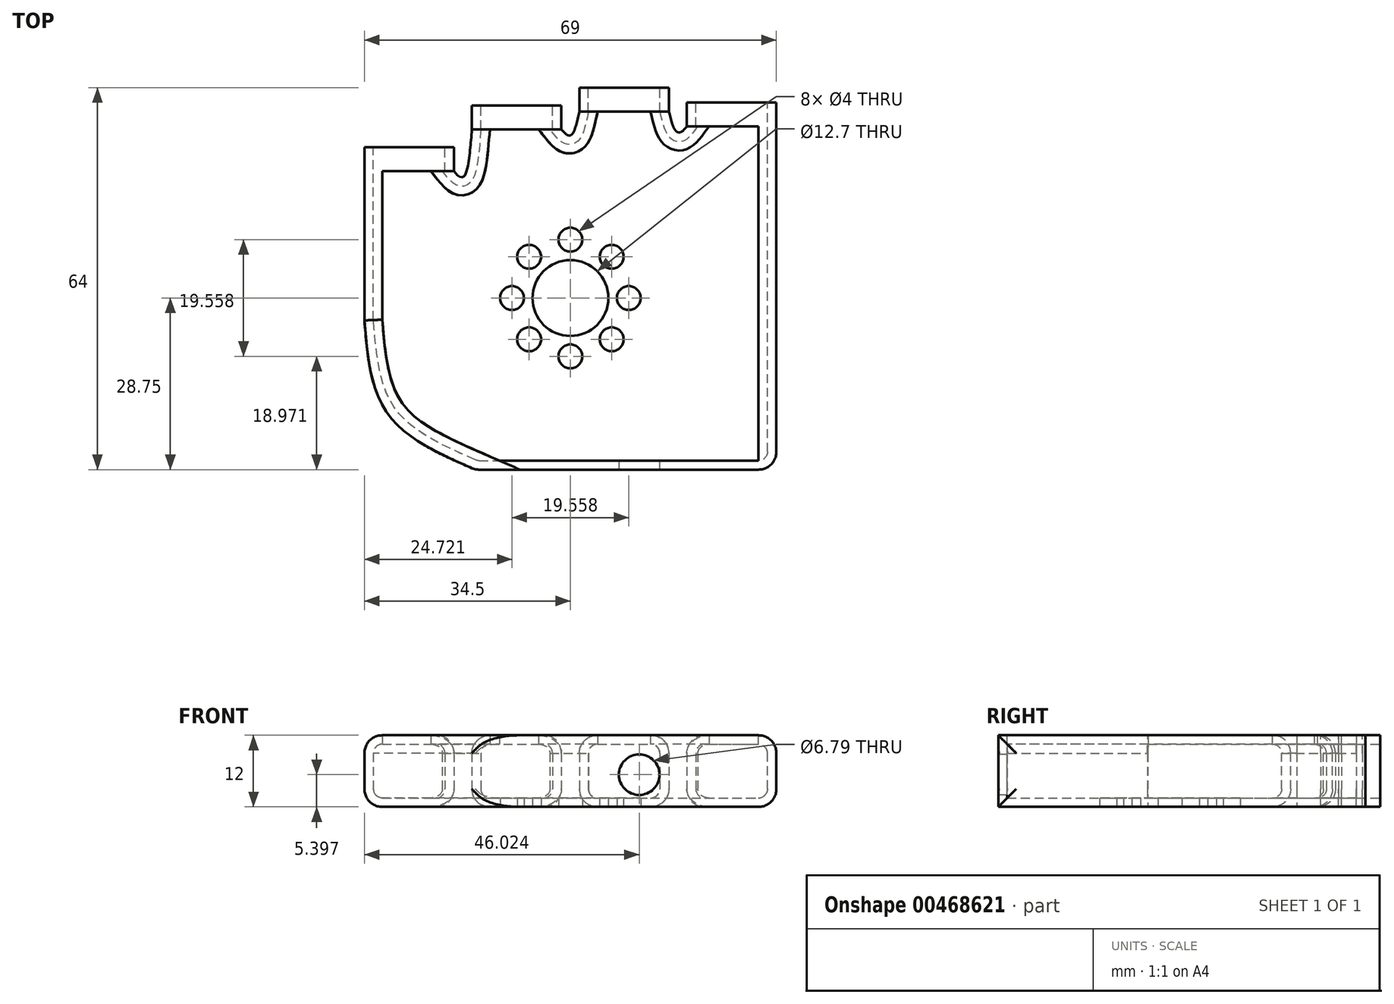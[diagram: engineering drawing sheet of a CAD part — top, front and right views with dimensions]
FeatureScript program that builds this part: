
annotation { "Feature Type Name" : "Feature", "Feature Type Description" : "" }
export const myFeature = defineFeature(function(context is Context, id is Id, definition is map)
    precondition{}
    {
        {
            assignVariable(context, id + "F0", {"name" : "finger_thickness", "anyValue" : 12 * mm});
        }
        {
            assignVariable(context, id + "F1", {"name" : "wall_thickness", "anyValue" : 1.5 * mm});
        }
        {
            var Q0;
            Q0=qCreatedBy(makeId("Top.planeOp"),FACE);
            var sketch = newSketch(context, id + "F2", { "sketchPlane" : qUnion([Q0])});
            skLineSegment(sketch, "E0.bottom", {"start": v(0, 0) * mm, "end": v(15, 0) * mm});
            skLineSegment(sketch, "E0.top", {"start": v(0, -4) * mm, "end": v(15, -4) * mm});
            skLineSegment(sketch, "E0.left", {"start": v(0, 0) * mm, "end": v(0, -4) * mm});
            skLineSegment(sketch, "E0.right", {"start": v(15, 0) * mm, "end": v(15, -4) * mm});
            skLineSegment(sketch, "E1.bottom", {"start": v(18, 7) * mm, "end": v(33, 7) * mm});
            skLineSegment(sketch, "E1.top", {"start": v(18, 3) * mm, "end": v(33, 3) * mm});
            skLineSegment(sketch, "E1.left", {"start": v(18, 7) * mm, "end": v(18, 3) * mm});
            skLineSegment(sketch, "E1.right", {"start": v(33, 7) * mm, "end": v(33, 3) * mm});
            skLineSegment(sketch, "E2.bottom", {"start": v(36, 10) * mm, "end": v(51, 10) * mm});
            skLineSegment(sketch, "E2.top", {"start": v(36, 6) * mm, "end": v(51, 6) * mm});
            skLineSegment(sketch, "E2.left", {"start": v(36, 10) * mm, "end": v(36, 6) * mm});
            skLineSegment(sketch, "E2.right", {"start": v(51, 10) * mm, "end": v(51, 6) * mm});
            skLineSegment(sketch, "E3.bottom", {"start": v(54, 7.5) * mm, "end": v(69, 7.5) * mm});
            skLineSegment(sketch, "E3.top", {"start": v(54, 3.5) * mm, "end": v(69, 3.5) * mm});
            skLineSegment(sketch, "E3.left", {"start": v(54, 7.5) * mm, "end": v(54, 3.5) * mm});
            skLineSegment(sketch, "E3.right", {"start": v(69, 7.5) * mm, "end": v(69, 3.5) * mm});
            skLineSegment(sketch, "E4", {"start": v(15, -4) * mm, "end": v(18, -4) * mm, "construction": true});
            skLineSegment(sketch, "E5", {"start": v(18, -4) * mm, "end": v(18, 3) * mm, "construction": true});
            skLineSegment(sketch, "E6", {"start": v(33, 3) * mm, "end": v(36, 3) * mm, "construction": true});
            skPoint(sketch, "E6.endSnap0", {"position": v(25.5, 3) * mm});
            skLineSegment(sketch, "E7", {"start": v(36, 3) * mm, "end": v(36, 6) * mm, "construction": true});
            skLineSegment(sketch, "E8", {"start": v(54, 3.5) * mm, "end": v(51, 3.5) * mm, "construction": true});
            skLineSegment(sketch, "E9", {"start": v(51, 3.5) * mm, "end": v(51, 6) * mm, "construction": true});
            skPoint(sketch, "E10.1.internal.snap0", {"position": v(16.5, -4) * mm});
            skFitSpline(sketch, "E10", {"points": [v(15, -4) * mm, v(16.5, -5) * mm, v(18, 3) * mm], "startDerivative": vector(5.03, -6.13) * mm, "endDerivative": vector(1.4, 17.37) * mm});
            skPoint(sketch, "E11.1.internal.snap0", {"position": v(34.5, 3) * mm});
            skFitSpline(sketch, "E11", {"points": [v(33, 3) * mm, v(34.5, 2) * mm, v(36, 6) * mm], "startDerivative": vector(4.04, -5) * mm, "endDerivative": vector(2.1, 9.97) * mm});
            skPoint(sketch, "E12.1.internal.snap0", {"position": v(52.5, 3.5) * mm});
            skFitSpline(sketch, "E12", {"points": [v(54, 3.5) * mm, v(52.5, 2.5) * mm, v(51, 6) * mm], "startDerivative": vector(-3.87, -5.3) * mm, "endDerivative": vector(-2.23, 9.44) * mm});
            skLineSegment(sketch, "E13", {"start": v(16.5, -4) * mm, "end": v(16.5, -5) * mm, "construction": true});
            skLineSegment(sketch, "E14", {"start": v(34.5, 3) * mm, "end": v(34.5, 2) * mm, "construction": true});
            skLineSegment(sketch, "E15", {"start": v(52.5, 3.5) * mm, "end": v(52.5, 2.5) * mm, "construction": true});
            skLineSegment(sketch, "E16", {"start": v(0, -4) * mm, "end": v(0, -54) * mm});
            skLineSegment(sketch, "E17", {"start": v(0, -54) * mm, "end": v(69, -54) * mm});
            skLineSegment(sketch, "E18", {"start": v(69, -54) * mm, "end": v(69, 3.5) * mm});
            skCircle(sketch, "E19", {"center": v(34.5, -25.25) * mm, "radius": 6.35 * mm});
            skPoint(sketch, "E19.centerSnap0", {"position": v(69, -25.25) * mm});
            skPoint(sketch, "E19.centerSnap1", {"position": v(34.5, -54) * mm});
            skCircle(sketch, "E20", {"center": v(34.5, -35.03) * mm, "radius": 2 * mm});
            skCircle(sketch, "E21.1.0", {"center": v(41.41, -32.16) * mm, "radius": 2 * mm});
            skCircle(sketch, "E21.2.0", {"center": v(44.28, -25.25) * mm, "radius": 2 * mm});
            skCircle(sketch, "E22.1.3.0", {"center": v(41.41, -18.34) * mm, "radius": 2 * mm});
            skCircle(sketch, "E22.1.4.0", {"center": v(34.5, -15.47) * mm, "radius": 2 * mm});
            skCircle(sketch, "E22.1.5.0", {"center": v(27.59, -18.34) * mm, "radius": 2 * mm});
            skCircle(sketch, "E22.1.6.0", {"center": v(24.72, -25.25) * mm, "radius": 2 * mm});
            skCircle(sketch, "E22.1.7.0", {"center": v(27.59, -32.16) * mm, "radius": 2 * mm});
            skFitSpline(sketch, "E23", {"points": [v(0, -29) * mm, v(3.91, -44.65) * mm, v(18.57, -54) * mm], "startDerivative": vector(2.88, -35.2) * mm, "endDerivative": vector(34.07, -14.92) * mm});
            skSolve(sketch);
        }
        {
            var Q0;
            Q0=makeQuery(id+"F2.imprint","IMPRINT",FACE,{"disambiguationData":[TD([[makeQuery(id+"F2.imprint","IMPRINT",EDGE,{"derivedFrom":sQuery(id+"F2.wireOp",EDGE,"E0.top")}),-1.0]])]});
            var Q1;
            Q1=makeQuery(id+"F2.imprint","IMPRINT",FACE,{"disambiguationData":[TD([[makeQuery(id+"F2.imprint","IMPRINT",EDGE,{"derivedFrom":sQuery(id+"F2.wireOp",EDGE,"E22.1.5.0")}),1.0]])]});
            var Q2;
            Q2=makeQuery(id+"F2.imprint","IMPRINT",FACE,{"disambiguationData":[TD([[makeQuery(id+"F2.imprint","IMPRINT",EDGE,{"derivedFrom":sQuery(id+"F2.wireOp",EDGE,"E22.1.6.0")}),1.0]])]});
            var Q3;
            Q3=makeQuery(id+"F2.imprint","IMPRINT",FACE,{"disambiguationData":[TD([[makeQuery(id+"F2.imprint","IMPRINT",EDGE,{"derivedFrom":sQuery(id+"F2.wireOp",EDGE,"E22.1.7.0")}),1.0]])]});
            var Q4;
            Q4=makeQuery(id+"F2.imprint","IMPRINT",FACE,{"disambiguationData":[TD([[makeQuery(id+"F2.imprint","IMPRINT",EDGE,{"derivedFrom":sQuery(id+"F2.wireOp",EDGE,"E20")}),1.0]])]});
            var Q5;
            Q5=makeQuery(id+"F2.imprint","IMPRINT",FACE,{"disambiguationData":[TD([[makeQuery(id+"F2.imprint","IMPRINT",EDGE,{"derivedFrom":sQuery(id+"F2.wireOp",EDGE,"E21.1.0")}),1.0]])]});
            var Q6;
            Q6=makeQuery(id+"F2.imprint","IMPRINT",FACE,{"disambiguationData":[TD([[makeQuery(id+"F2.imprint","IMPRINT",EDGE,{"derivedFrom":sQuery(id+"F2.wireOp",EDGE,"E21.2.0")}),1.0]])]});
            var Q7;
            Q7=makeQuery(id+"F2.imprint","IMPRINT",FACE,{"disambiguationData":[TD([[makeQuery(id+"F2.imprint","IMPRINT",EDGE,{"derivedFrom":sQuery(id+"F2.wireOp",EDGE,"E22.1.3.0")}),1.0]])]});
            var Q8;
            Q8=makeQuery(id+"F2.imprint","IMPRINT",FACE,{"disambiguationData":[TD([[makeQuery(id+"F2.imprint","IMPRINT",EDGE,{"derivedFrom":sQuery(id+"F2.wireOp",EDGE,"E22.1.4.0")}),1.0]])]});
            var Q9;
            Q9=makeQuery(id+"F2.imprint","IMPRINT",FACE,{"disambiguationData":[TD([[makeQuery(id+"F2.imprint","IMPRINT",EDGE,{"derivedFrom":sQuery(id+"F2.wireOp",EDGE,"E19")}),1.0]])]});
            extrude(context, id + "F3", {"entities" : qUnion([Q0, Q1, Q2, Q3, Q4, Q5, Q6, Q7, Q8, Q9]), "depth" : getVariable(context, 'finger_thickness'), "offsetDistance" : 25 * mm});
        }
        {
            var Q0;
            Q0=makeQuery(id+"F3.opExtrude","CAP_EDGE",EDGE,{"disambiguationData":[OSD([sQuery(id+"F2.wireOp",EDGE,"E0.left"),sQuery(id+"F2.wireOp",EDGE,"E16")])],"isStart":false});
            var Q1;
            Q1=makeQuery(id+"F3.opExtrude","CAP_EDGE",EDGE,{"disambiguationData":[OSD([sQuery(id+"F2.wireOp",EDGE,"E0.left"),sQuery(id+"F2.wireOp",EDGE,"E16")])],"isStart":true});
            var Q2;
            Q2=makeQuery(id+"F3.opExtrude","CAP_EDGE",EDGE,{"disambiguationData":[OSD([sQuery(id+"F2.wireOp",EDGE,"E3.right"),sQuery(id+"F2.wireOp",EDGE,"E18")])],"isStart":false});
            var Q3;
            Q3=makeQuery(id+"F3.opExtrude","CAP_EDGE",EDGE,{"disambiguationData":[OSD([sQuery(id+"F2.wireOp",EDGE,"E11")])],"isStart":false});
            var Q4;
            Q4=makeQuery(id+"F3.opExtrude","CAP_EDGE",EDGE,{"disambiguationData":[OSD([sQuery(id+"F2.wireOp",EDGE,"E10")])],"isStart":false});
            var Q5;
            Q5=makeQuery(id+"F3.opExtrude","CAP_EDGE",EDGE,{"disambiguationData":[OSD([sQuery(id+"F2.wireOp",EDGE,"E12")])],"isStart":false});
            var Q6;
            Q6=makeQuery(id+"F3.opExtrude","CAP_EDGE",EDGE,{"disambiguationData":[OSD([sQuery(id+"F2.wireOp",EDGE,"E12")])],"isStart":true});
            var Q7;
            Q7=makeQuery(id+"F3.opExtrude","CAP_EDGE",EDGE,{"disambiguationData":[OSD([sQuery(id+"F2.wireOp",EDGE,"E11")])],"isStart":true});
            var Q8;
            Q8=makeQuery(id+"F3.opExtrude","CAP_EDGE",EDGE,{"disambiguationData":[OSD([sQuery(id+"F2.wireOp",EDGE,"E10")])],"isStart":true});
            var Q9;
            Q9=makeQuery(id+"F3.opExtrude","CAP_EDGE",EDGE,{"disambiguationData":[OSD([sQuery(id+"F2.wireOp",EDGE,"E18")])],"isStart":true});
            var Q10;
            Q10=makeQuery(id+"F3.opExtrude","CAP_EDGE",EDGE,{"disambiguationData":[OSD([sQuery(id+"F2.wireOp",EDGE,"E23")])],"isStart":false});
            var Q11;
            Q11=makeQuery(id+"F3.opExtrude","CAP_EDGE",EDGE,{"disambiguationData":[OSD([sQuery(id+"F2.wireOp",EDGE,"E23")])],"isStart":true});
            var Q12;
            Q12=makeQuery(id+"F3.opExtrude","SWEPT_EDGE",EDGE,{"disambiguationData":[OSD([sQuery(id+"F2.wireOp",EDGE,"E17"),sQuery(id+"F2.wireOp",EDGE,"E23")])]});
            var Q13;
            Q13=makeQuery(id+"F3.opExtrude","SWEPT_EDGE",EDGE,{"disambiguationData":[OSD([sQuery(id+"F2.wireOp",EDGE,"E17"),sQuery(id+"F2.wireOp",EDGE,"E18")])]});
            fillet(context, id + "F4", {"entities" : qUnion([Q0, Q1, Q2, Q3, Q4, Q5, Q6, Q7, Q8, Q9, Q10, Q11, Q12, Q13]), "radius" : 3 * mm, "tangentPropagation" : true, "allowEdgeOverflow" : false});
        }
        {
            var Q0;
            Q0=makeQuery(id+"F3.opExtrude","CAP_FACE",FACE,{"disambiguationData":[OSD([sQuery(id+"F2.wireOp",EDGE,"E0.top"),sQuery(id+"F2.wireOp",EDGE,"E0.right"),sQuery(id+"F2.wireOp",EDGE,"E1.top"),sQuery(id+"F2.wireOp",EDGE,"E2.top"),sQuery(id+"F2.wireOp",EDGE,"E3.top"),sQuery(id+"F2.wireOp",EDGE,"E10"),sQuery(id+"F2.wireOp",EDGE,"E11"),sQuery(id+"F2.wireOp",EDGE,"E12"),sQuery(id+"F2.wireOp",EDGE,"E16"),sQuery(id+"F2.wireOp",EDGE,"E17"),sQuery(id+"F2.wireOp",EDGE,"E18")])],"isStart":false});
            var Q1;
            Q1=makeQuery(id+"F3.opExtrude","SWEPT_FACE",FACE,{"disambiguationData":[OSD([sQuery(id+"F2.wireOp",EDGE,"E3.top")])]});
            var Q2;
            Q2=makeQuery(id+"F3.opExtrude","SWEPT_FACE",FACE,{"disambiguationData":[OSD([sQuery(id+"F2.wireOp",EDGE,"E2.top")])]});
            var Q3;
            Q3=makeQuery(id+"F3.opExtrude","SWEPT_FACE",FACE,{"disambiguationData":[OSD([sQuery(id+"F2.wireOp",EDGE,"E1.top")])]});
            var Q4;
            Q4=makeQuery(id+"F3.opExtrude","SWEPT_FACE",FACE,{"disambiguationData":[OSD([sQuery(id+"F2.wireOp",EDGE,"E0.top")])]});
            shell(context, id + "F5", {"entities" : qUnion([Q0, Q1, Q2, Q3, Q4]), "thickness" : getVariable(context, 'wall_thickness')});
        }
        {
            var Q0;
            Q0=makeQuery(id+"F2.imprint","IMPRINT",FACE,{"disambiguationData":[TD([[makeQuery(id+"F2.imprint","IMPRINT",EDGE,{"derivedFrom":sQuery(id+"F2.wireOp",EDGE,"E0.bottom")}),-1.0]])]});
            var Q1;
            Q1=makeQuery(id+"F2.imprint","IMPRINT",FACE,{"disambiguationData":[TD([[makeQuery(id+"F2.imprint","IMPRINT",EDGE,{"derivedFrom":sQuery(id+"F2.wireOp",EDGE,"E1.bottom")}),-1.0]])]});
            var Q2;
            Q2=makeQuery(id+"F2.imprint","IMPRINT",FACE,{"disambiguationData":[TD([[makeQuery(id+"F2.imprint","IMPRINT",EDGE,{"derivedFrom":sQuery(id+"F2.wireOp",EDGE,"E2.bottom")}),-1.0]])]});
            var Q3;
            Q3=makeQuery(id+"F2.imprint","IMPRINT",FACE,{"disambiguationData":[TD([[makeQuery(id+"F2.imprint","IMPRINT",EDGE,{"derivedFrom":sQuery(id+"F2.wireOp",EDGE,"E3.bottom")}),-1.0]])]});
            extrude(context, id + "F6", {"entities" : qUnion([Q0, Q1, Q2, Q3]), "depth" : getVariable(context, 'finger_thickness'), "offsetDistance" : 25 * mm});
        }
        {
            var Q0;
            Q0=makeQuery(id+"F6.opExtrude","CAP_EDGE",EDGE,{"disambiguationData":[OSD([sQuery(id+"F2.wireOp",EDGE,"E0.left")])],"isStart":false});
            var Q1;
            Q1=makeQuery(id+"F6.opExtrude","CAP_EDGE",EDGE,{"disambiguationData":[OSD([sQuery(id+"F2.wireOp",EDGE,"E0.right")])],"isStart":false});
            var Q2;
            Q2=makeQuery(id+"F6.opExtrude","CAP_EDGE",EDGE,{"disambiguationData":[OSD([sQuery(id+"F2.wireOp",EDGE,"E0.left")])],"isStart":true});
            var Q3;
            Q3=makeQuery(id+"F6.opExtrude","CAP_EDGE",EDGE,{"disambiguationData":[OSD([sQuery(id+"F2.wireOp",EDGE,"E1.left")])],"isStart":false});
            var Q4;
            Q4=makeQuery(id+"F6.opExtrude","CAP_EDGE",EDGE,{"disambiguationData":[OSD([sQuery(id+"F2.wireOp",EDGE,"E1.right")])],"isStart":false});
            var Q5;
            Q5=makeQuery(id+"F6.opExtrude","CAP_EDGE",EDGE,{"disambiguationData":[OSD([sQuery(id+"F2.wireOp",EDGE,"E2.left")])],"isStart":false});
            var Q6;
            Q6=makeQuery(id+"F6.opExtrude","CAP_EDGE",EDGE,{"disambiguationData":[OSD([sQuery(id+"F2.wireOp",EDGE,"E2.right")])],"isStart":false});
            var Q7;
            Q7=makeQuery(id+"F6.opExtrude","CAP_EDGE",EDGE,{"disambiguationData":[OSD([sQuery(id+"F2.wireOp",EDGE,"E3.left")])],"isStart":false});
            var Q8;
            Q8=makeQuery(id+"F6.opExtrude","CAP_EDGE",EDGE,{"disambiguationData":[OSD([sQuery(id+"F2.wireOp",EDGE,"E3.right")])],"isStart":false});
            var Q9;
            Q9=makeQuery(id+"F6.opExtrude","CAP_EDGE",EDGE,{"disambiguationData":[OSD([sQuery(id+"F2.wireOp",EDGE,"E3.right")])],"isStart":true});
            var Q10;
            Q10=makeQuery(id+"F6.opExtrude","CAP_EDGE",EDGE,{"disambiguationData":[OSD([sQuery(id+"F2.wireOp",EDGE,"E0.right")])],"isStart":true});
            var Q11;
            Q11=makeQuery(id+"F6.opExtrude","CAP_EDGE",EDGE,{"disambiguationData":[OSD([sQuery(id+"F2.wireOp",EDGE,"E1.right")])],"isStart":true});
            var Q12;
            Q12=makeQuery(id+"F6.opExtrude","CAP_EDGE",EDGE,{"disambiguationData":[OSD([sQuery(id+"F2.wireOp",EDGE,"E2.right")])],"isStart":true});
            var Q13;
            Q13=makeQuery(id+"F6.opExtrude","CAP_EDGE",EDGE,{"disambiguationData":[OSD([sQuery(id+"F2.wireOp",EDGE,"E1.left")])],"isStart":true});
            var Q14;
            Q14=makeQuery(id+"F6.opExtrude","CAP_EDGE",EDGE,{"disambiguationData":[OSD([sQuery(id+"F2.wireOp",EDGE,"E2.left")])],"isStart":true});
            var Q15;
            Q15=makeQuery(id+"F6.opExtrude","CAP_EDGE",EDGE,{"disambiguationData":[OSD([sQuery(id+"F2.wireOp",EDGE,"E3.left")])],"isStart":true});
            fillet(context, id + "F7", {"entities" : qUnion([Q0, Q1, Q2, Q3, Q4, Q5, Q6, Q7, Q8, Q9, Q10, Q11, Q12, Q13, Q14, Q15]), "radius" : 3 * mm, "tangentPropagation" : true, "allowEdgeOverflow" : false});
        }
        {
            var Q0;
            Q0=makeQuery(id+"F6.opExtrude","SWEPT_FACE",FACE,{"disambiguationData":[OSD([sQuery(id+"F2.wireOp",EDGE,"E0.top")])]});
            var Q1;
            Q1=makeQuery(id+"F6.opExtrude","SWEPT_FACE",FACE,{"disambiguationData":[OSD([sQuery(id+"F2.wireOp",EDGE,"E1.top")])]});
            var Q2;
            Q2=makeQuery(id+"F6.opExtrude","SWEPT_FACE",FACE,{"disambiguationData":[OSD([sQuery(id+"F2.wireOp",EDGE,"E2.top")])]});
            var Q3;
            Q3=makeQuery(id+"F6.opExtrude","SWEPT_FACE",FACE,{"disambiguationData":[OSD([sQuery(id+"F2.wireOp",EDGE,"E3.top")])]});
            var Q4;
            Q4=makeQuery(id+"F6.opExtrude","SWEPT_FACE",FACE,{"disambiguationData":[OSD([sQuery(id+"F2.wireOp",EDGE,"E0.bottom")])]});
            var Q5;
            Q5=makeQuery(id+"F6.opExtrude","SWEPT_FACE",FACE,{"disambiguationData":[OSD([sQuery(id+"F2.wireOp",EDGE,"E1.bottom")])]});
            var Q6;
            Q6=makeQuery(id+"F6.opExtrude","SWEPT_FACE",FACE,{"disambiguationData":[OSD([sQuery(id+"F2.wireOp",EDGE,"E2.bottom")])]});
            var Q7;
            Q7=makeQuery(id+"F6.opExtrude","SWEPT_FACE",FACE,{"disambiguationData":[OSD([sQuery(id+"F2.wireOp",EDGE,"E3.bottom")])]});
            shell(context, id + "F8", {"entities" : qUnion([Q0, Q1, Q2, Q3, Q4, Q5, Q6, Q7]), "thickness" : getVariable(context, 'wall_thickness')});
        }
        {
            var Q0;
            Q0=makeQuery(id+"F3.opExtrude","SWEPT_BODY",BODY,{"disambiguationData":[OSD([sQuery(id+"F2.wireOp",EDGE,"E0.top"),sQuery(id+"F2.wireOp",EDGE,"E1.top"),sQuery(id+"F2.wireOp",EDGE,"E2.top"),sQuery(id+"F2.wireOp",EDGE,"E3.top"),sQuery(id+"F2.wireOp",EDGE,"E10"),sQuery(id+"F2.wireOp",EDGE,"E11"),sQuery(id+"F2.wireOp",EDGE,"E12"),sQuery(id+"F2.wireOp",EDGE,"E16"),sQuery(id+"F2.wireOp",EDGE,"E17"),sQuery(id+"F2.wireOp",EDGE,"E18")])]});
            var Q1;
            Q1=makeQuery(id+"F6.opExtrude","SWEPT_BODY",BODY,{"disambiguationData":[OSD([sQuery(id+"F2.wireOp",EDGE,"E0.bottom"),sQuery(id+"F2.wireOp",EDGE,"E0.top"),sQuery(id+"F2.wireOp",EDGE,"E0.left"),sQuery(id+"F2.wireOp",EDGE,"E0.right")])]});
            var Q2;
            Q2=makeQuery(id+"F6.opExtrude","SWEPT_BODY",BODY,{"disambiguationData":[OSD([sQuery(id+"F2.wireOp",EDGE,"E1.bottom"),sQuery(id+"F2.wireOp",EDGE,"E1.top"),sQuery(id+"F2.wireOp",EDGE,"E1.left"),sQuery(id+"F2.wireOp",EDGE,"E1.right")])]});
            var Q3;
            Q3=makeQuery(id+"F6.opExtrude","SWEPT_BODY",BODY,{"disambiguationData":[OSD([sQuery(id+"F2.wireOp",EDGE,"E2.bottom"),sQuery(id+"F2.wireOp",EDGE,"E2.top"),sQuery(id+"F2.wireOp",EDGE,"E2.left"),sQuery(id+"F2.wireOp",EDGE,"E2.right")])]});
            var Q4;
            Q4=makeQuery(id+"F6.opExtrude","SWEPT_BODY",BODY,{"disambiguationData":[OSD([sQuery(id+"F2.wireOp",EDGE,"E3.bottom"),sQuery(id+"F2.wireOp",EDGE,"E3.top"),sQuery(id+"F2.wireOp",EDGE,"E3.left"),sQuery(id+"F2.wireOp",EDGE,"E3.right")])]});
            booleanBodies(context, id + "F9", {"operationType" : BooleanOperationType.UNION, "tools" : qUnion([Q0, Q1, Q2, Q3, Q4])});
        }
        {
            var Q0;
            Q0=makeQuery(id+"F3.opExtrude","SWEPT_FACE",FACE,{"disambiguationData":[OSD([sQuery(id+"F2.wireOp",EDGE,"E17")])]});
            var sketch = newSketch(context, id + "F10", { "sketchPlane" : qUnion([Q0])});
            skCircle(sketch, "E24", {"center": v(46.02, 5.4) * mm, "radius": 3.4 * mm});
            skPoint(sketch, "E24.centerSnap0", {"position": v(46.02, 0) * mm});
            skSolve(sketch);
        }
        {
            var Q0;
            Q0=makeQuery(id+"F10.imprint","IMPRINT",FACE,{"disambiguationData":[TD([[makeQuery(id+"F10.imprint","IMPRINT",EDGE,{"derivedFrom":sQuery(id+"F10.wireOp",EDGE,"E24")}),1.0]])]});
            var Q1;
            Q1=makeQuery(id+"F5.opShell","OFFSET_FACE",FACE,{"disambiguationData":[OSD([sQuery(id+"F2.wireOp",EDGE,"E17")])]});
            extrude(context, id + "F11", {"entities" : qUnion([Q0]), "operationType" : NewBodyOperationType.REMOVE, "endBound" : BoundingType.UP_TO_SURFACE, "oppositeDirection" : true, "depth" : 25 * mm, "endBoundEntityFace" : qUnion([Q1]), "offsetDistance" : 25 * mm});
        }
        {
            var Q0;
            Q0=makeQuery(id+"F2.imprint","IMPRINT",FACE,{"disambiguationData":[TD([[makeQuery(id+"F2.imprint","IMPRINT",EDGE,{"derivedFrom":sQuery(id+"F2.wireOp",EDGE,"E20")}),1.0]])]});
            var Q1;
            Q1=makeQuery(id+"F2.imprint","IMPRINT",FACE,{"disambiguationData":[TD([[makeQuery(id+"F2.imprint","IMPRINT",EDGE,{"derivedFrom":sQuery(id+"F2.wireOp",EDGE,"E21.1.0")}),1.0]])]});
            var Q2;
            Q2=makeQuery(id+"F2.imprint","IMPRINT",FACE,{"disambiguationData":[TD([[makeQuery(id+"F2.imprint","IMPRINT",EDGE,{"derivedFrom":sQuery(id+"F2.wireOp",EDGE,"E21.2.0")}),1.0]])]});
            var Q3;
            Q3=makeQuery(id+"F2.imprint","IMPRINT",FACE,{"disambiguationData":[TD([[makeQuery(id+"F2.imprint","IMPRINT",EDGE,{"derivedFrom":sQuery(id+"F2.wireOp",EDGE,"E22.1.3.0")}),1.0]])]});
            var Q4;
            Q4=makeQuery(id+"F2.imprint","IMPRINT",FACE,{"disambiguationData":[TD([[makeQuery(id+"F2.imprint","IMPRINT",EDGE,{"derivedFrom":sQuery(id+"F2.wireOp",EDGE,"E22.1.4.0")}),1.0]])]});
            var Q5;
            Q5=makeQuery(id+"F2.imprint","IMPRINT",FACE,{"disambiguationData":[TD([[makeQuery(id+"F2.imprint","IMPRINT",EDGE,{"derivedFrom":sQuery(id+"F2.wireOp",EDGE,"E22.1.6.0")}),1.0]])]});
            var Q6;
            Q6=makeQuery(id+"F2.imprint","IMPRINT",FACE,{"disambiguationData":[TD([[makeQuery(id+"F2.imprint","IMPRINT",EDGE,{"derivedFrom":sQuery(id+"F2.wireOp",EDGE,"E22.1.5.0")}),1.0]])]});
            var Q7;
            Q7=makeQuery(id+"F2.imprint","IMPRINT",FACE,{"disambiguationData":[TD([[makeQuery(id+"F2.imprint","IMPRINT",EDGE,{"derivedFrom":sQuery(id+"F2.wireOp",EDGE,"E22.1.7.0")}),1.0]])]});
            var Q8;
            Q8=makeQuery(id+"F2.imprint","IMPRINT",FACE,{"disambiguationData":[TD([[makeQuery(id+"F2.imprint","IMPRINT",EDGE,{"derivedFrom":sQuery(id+"F2.wireOp",EDGE,"E19")}),1.0]])]});
            var Q9;
            {var subQ0=sQuery(id+"F2.wireOp",EDGE,"E3.right");var subQ1=sQuery(id+"F2.wireOp",EDGE,"E3.left");var subQ2=sQuery(id+"F2.wireOp",EDGE,"E3.top");var subQ3=sQuery(id+"F2.wireOp",EDGE,"E3.bottom");var subQ4=sQuery(id+"F2.wireOp",EDGE,"E2.right");var subQ5=sQuery(id+"F2.wireOp",EDGE,"E2.left");var subQ6=sQuery(id+"F2.wireOp",EDGE,"E2.top");var subQ7=sQuery(id+"F2.wireOp",EDGE,"E2.bottom");var subQ8=sQuery(id+"F2.wireOp",EDGE,"E1.right");var subQ9=sQuery(id+"F2.wireOp",EDGE,"E1.left");var subQ10=sQuery(id+"F2.wireOp",EDGE,"E1.top");var subQ11=sQuery(id+"F2.wireOp",EDGE,"E1.bottom");var subQ12=sQuery(id+"F2.wireOp",EDGE,"E0.right");var subQ13=sQuery(id+"F2.wireOp",EDGE,"E0.left");var subQ14=sQuery(id+"F2.wireOp",EDGE,"E0.top");var subQ15=sQuery(id+"F2.wireOp",EDGE,"E0.bottom");Q9=makeQuery(id+"F9.opBoolean","MERGE",FACE,{"derivedFrom":[makeQuery(id+"F5.opShell","OFFSET_FACE",FACE,{"disambiguationData":[OSD([subQ14,subQ10,subQ6,subQ2,sQuery(id+"F2.wireOp",EDGE,"E10"),sQuery(id+"F2.wireOp",EDGE,"E11"),sQuery(id+"F2.wireOp",EDGE,"E12"),sQuery(id+"F2.wireOp",EDGE,"E16"),sQuery(id+"F2.wireOp",EDGE,"E17"),sQuery(id+"F2.wireOp",EDGE,"E18")])]}),makeQuery(id+"F8.opShell","OFFSET_FACE",FACE,{"disambiguationData":[OSD([subQ15,subQ14,subQ13,subQ12]),TDD([makeQuery(id+"F6.opExtrude","CAP_FACE",FACE,{"disambiguationData":[OSD([subQ15,subQ14,subQ13,subQ12])],"isStart":true})])]}),makeQuery(id+"F8.opShell","OFFSET_FACE",FACE,{"disambiguationData":[OSD([subQ11,subQ10,subQ9,subQ8]),TDD([makeQuery(id+"F6.opExtrude","CAP_FACE",FACE,{"disambiguationData":[OSD([subQ11,subQ10,subQ9,subQ8])],"isStart":true})])]}),makeQuery(id+"F8.opShell","OFFSET_FACE",FACE,{"disambiguationData":[OSD([subQ7,subQ6,subQ5,subQ4]),TDD([makeQuery(id+"F6.opExtrude","CAP_FACE",FACE,{"disambiguationData":[OSD([subQ7,subQ6,subQ5,subQ4])],"isStart":true})])]}),makeQuery(id+"F8.opShell","OFFSET_FACE",FACE,{"disambiguationData":[OSD([subQ3,subQ2,subQ1,subQ0]),TDD([makeQuery(id+"F6.opExtrude","CAP_FACE",FACE,{"disambiguationData":[OSD([subQ3,subQ2,subQ1,subQ0])],"isStart":true})])]})]});}
            extrude(context, id + "F12", {"entities" : qUnion([Q0, Q1, Q2, Q3, Q4, Q5, Q6, Q7, Q8]), "operationType" : NewBodyOperationType.REMOVE, "endBound" : BoundingType.UP_TO_SURFACE, "depth" : 25 * mm, "endBoundEntityFace" : qUnion([Q9]), "offsetDistance" : 25 * mm});
        }
    });
